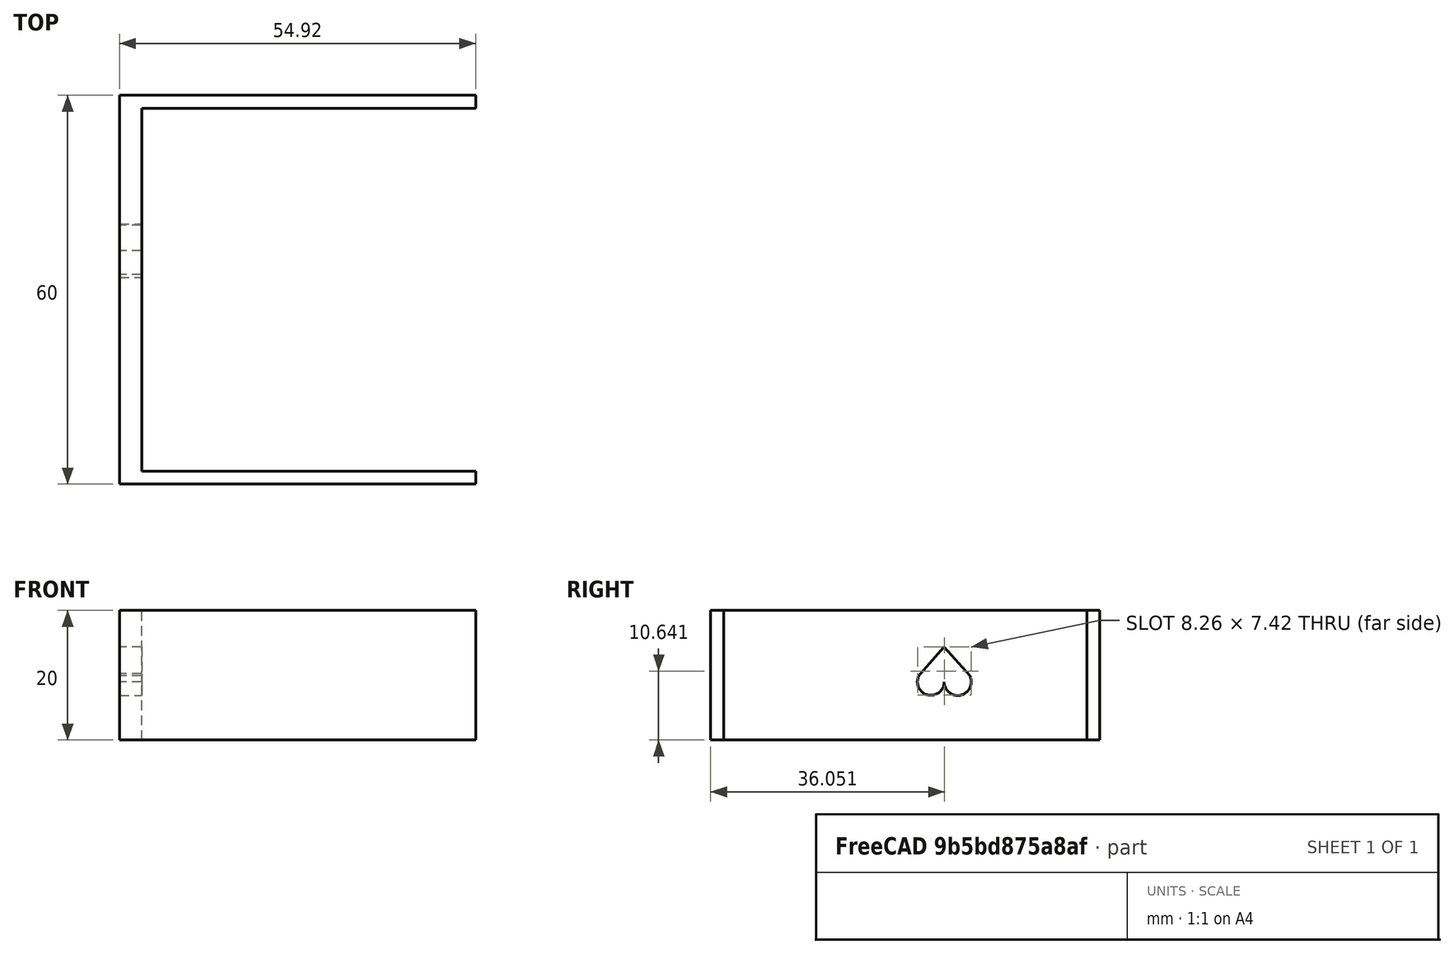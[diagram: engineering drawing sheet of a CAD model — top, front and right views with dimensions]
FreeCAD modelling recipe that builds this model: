
FCSTD DOCUMENT  (FreeCAD 1.0R39109 (Git))
Label: heart
License: All rights reserved
LicenseURL: https://en.wikipedia.org/wiki/All_rights_reserved
objects: Sketcher::SketchObject×3, Part::Extrusion×3, Part::Cut×2, Mesh::Feature×1, App::DocumentObjectGroup×1
note: 11 computed .brp shape members not serialized (recipe doc carries the construction recipe); baked Part::Feature solids carry a one-line shape summary decoded from their .brp

FEATURE [Mesh::Feature] bottom_esp35_battery
  Placement = pos=(0,1.5,0) rot=(0,0,1;0rad)
FEATURE [Sketcher::SketchObject] Sketch
  ArcFitTolerance = 1e-06
  FullyConstrained = false
  MakeInternals = false
  sketch-geometry (4):
    g0: LineSegment StartX=-41.6929 StartY=-30 StartZ=0 EndX=13.2309 EndY=-30 EndZ=0
    g1: LineSegment StartX=13.2309 StartY=-30 StartZ=0 EndX=13.2309 EndY=30 EndZ=0
    g2: LineSegment StartX=13.2309 StartY=30 StartZ=0 EndX=-41.6929 EndY=30 EndZ=0
    g3: LineSegment StartX=-41.6929 StartY=30 StartZ=0 EndX=-41.6929 EndY=-30 EndZ=0
  constraints (10):
    c: Coincident(g0,g1)
    c: Coincident(g1,g2)
    c: Coincident(g2,g3)
    c: Coincident(g3,g0)
    c: Horizontal(g0)
    c: Horizontal(g2)
    c: Vertical(g1)
    c: Vertical(g3)
    c: Distance(g-1,g2) = 30
    c: Distance(g-1,g0) = 30
FEATURE [Sketcher::SketchObject] Sketch001
  ArcFitTolerance = 1e-06
  AttachmentSupport = -> [Sketch]
  FullyConstrained = false
  MakeInternals = false
  MapMode = 2
  sketch-geometry (4):
    g0: LineSegment StartX=-38.27 StartY=28 StartZ=0 EndX=-38.27 EndY=-28 EndZ=0
    g1: LineSegment StartX=-38.27 StartY=-28 StartZ=0 EndX=54.4221 EndY=-28 EndZ=0
    g2: LineSegment StartX=54.4221 StartY=-28 StartZ=0 EndX=54.4221 EndY=28 EndZ=0
    g3: LineSegment StartX=54.4221 StartY=28 StartZ=0 EndX=-38.27 EndY=28 EndZ=0
  constraints (10):
    c: Coincident(g0,g1)
    c: Coincident(g1,g2)
    c: Coincident(g2,g3)
    c: Coincident(g3,g0)
    c: Vertical(g0)
    c: Vertical(g2)
    c: Horizontal(g1)
    c: Horizontal(g3)
    c: Distance(g-1,g3) = 28
    c: Distance(g-1,g1) = 28
FEATURE [Part::Extrusion] Extrude
  Base = -> Sketch
  Dir = (0,0,1)
  DirMode = 2
  FaceMakerClass = Part::FaceMakerBullseye
  FaceMakerMode = 3
  LengthFwd = 10
  LengthRev = 10
  Solid = true
  Symmetric = false
FEATURE [Part::Extrusion] Extrude001
  Base = -> Sketch001
  Dir = (0,0,1)
  DirMode = 2
  FaceMakerClass = Part::FaceMakerBullseye
  FaceMakerMode = 3
  LengthFwd = 10
  LengthRev = 10
  Solid = true
  Symmetric = false
FEATURE [Part::Cut] Cut
  Base = -> Extrude
  Tool = -> Extrude001
FEATURE [App::DocumentObjectGroup] Measurements
FEATURE [Sketcher::SketchObject] Sketch004
  ArcFitTolerance = 1e-06
  AttachmentSupport = -> [Cut]
  FullyConstrained = false
  MakeInternals = false
  MapMode = 5
  Placement = pos=(-41.6929,0,0) rot=(0.57735,-0.57735,-0.57735;2.0944rad)
  sketch-geometry (5):
    g0: GeomPoint [constr] X=-6 Y=0 Z=0
    g1: LineSegment StartX=-6 StartY=4.35232 StartZ=0 EndX=-9.95335 EndY=-0.0777847 EndZ=0
    g2: LineSegment StartX=-6 StartY=4.35232 StartZ=0 EndX=-2.33637 EndY=0.268381 EndZ=0
    g3: ArcOfCircle CenterX=-3.93945 CenterY=-1.02637 CenterZ=0 NormalX=0 NormalY=0 NormalZ=1 AngleXU=0 Radius=2.06065 StartAngle=3.1513 EndAngle=6.96258
    g4: ArcOfCircle CenterX=-8.09043 CenterY=-1.02637 CenterZ=0 NormalX=0 NormalY=0 NormalZ=1 AngleXU=0 Radius=2.09052 StartAngle=2.67062 EndAngle=6.27361
  constraints (9):
    c: PointOnObject(g0,g-1)
    c: DistanceX(g0,g-1) = 6
    c: Coincident(g2,g1)
    c: Coincident(g3,g2)
    c: Coincident(g4,g1)
    c: Coincident(g4,g3)
    c: DistanceY(g4,g3) = 0
    c: DistanceX(g0,g3) = 0
    c: DistanceX(g1,g0) = 0
FEATURE [Part::Extrusion] Extrude002
  Base = -> Sketch004
  Dir = (-1,0,0)
  DirMode = 2
  FaceMakerClass = Part::FaceMakerBullseye
  FaceMakerMode = 3
  LengthFwd = 10
  LengthRev = 10
  Solid = true
  Symmetric = false
FEATURE [Part::Cut] Cut001
  Base = -> Cut
  Tool = -> Extrude002
